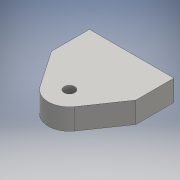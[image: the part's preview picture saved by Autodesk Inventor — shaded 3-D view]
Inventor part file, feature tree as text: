
AUTODESK INVENTOR PART (.ipt)
format: ipt  version: 2016 SP1 (Build 200210100, 210)  size: 96,256 bytes
history: native  units: mm
features: extrude x1, sketch x1
ambient origin geometry x8: Origin, YZ Plane, XZ Plane, XY Plane, X Axis, Y Axis, Z Axis, Center Point
bodies: Solid1 (feature_tree)
feature tree (2):
  extrude  "Extrusion1"  Depth=10.0mm
  sketch  "Sketch1"  dims[d0=5.0mm d1=29.5mm d2=40.0mm d3=20.0mm d4=18.0mm d5=20.0mm d6=10.0mm d7=0.0mm]
